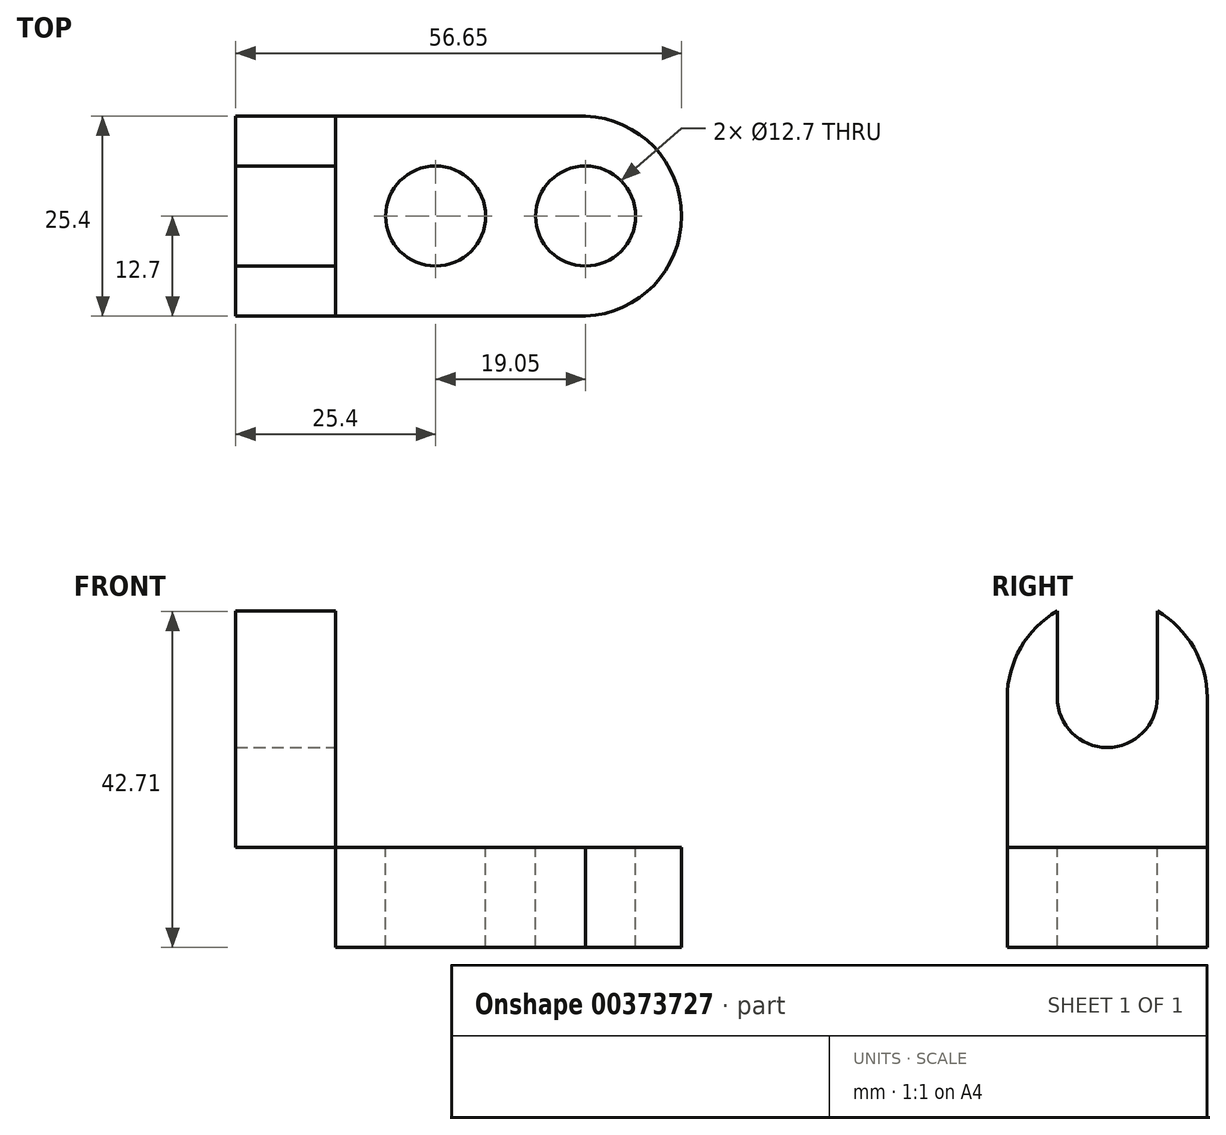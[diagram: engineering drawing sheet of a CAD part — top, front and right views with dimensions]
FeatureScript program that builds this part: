
annotation { "Feature Type Name" : "Feature", "Feature Type Description" : "" }
export const myFeature = defineFeature(function(context is Context, id is Id, definition is map)
    precondition{}
    {
        {
            var Q0;
            Q0=qCreatedBy(makeId("Front.planeOp"),FACE);
            var sketch = newSketch(context, id + "F0", { "sketchPlane" : qUnion([Q0])});
            skLineSegment(sketch, "E0.bottom", {"start": v(0, 0) * mm, "end": v(12.7, 0) * mm});
            skLineSegment(sketch, "E0.top", {"start": v(0, 44.45) * mm, "end": v(12.7, 44.45) * mm});
            skLineSegment(sketch, "E0.left", {"start": v(0, 0) * mm, "end": v(0, 44.45) * mm});
            skLineSegment(sketch, "E0.right", {"start": v(12.7, 0) * mm, "end": v(12.7, 44.45) * mm});
            skLineSegment(sketch, "E1.bottom", {"start": v(0, 0) * mm, "end": v(57.15, 0) * mm});
            skLineSegment(sketch, "E1.top", {"start": v(0, 12.7) * mm, "end": v(57.15, 12.7) * mm});
            skLineSegment(sketch, "E1.left", {"start": v(0, 0) * mm, "end": v(0, 12.7) * mm});
            skLineSegment(sketch, "E1.right", {"start": v(57.15, 0) * mm, "end": v(57.15, 12.7) * mm});
            skSolve(sketch);
        }
        {
            var Q0;
            {var subQ0=sQuery(id+"F0.wireOp",EDGE,"E0.top");Q0=makeQuery(id+"F0.imprint","IMPRINT",FACE,{"disambiguationData":[TD([[makeQuery(id+"F0.imprint","IMPRINT",EDGE,{"derivedFrom":subQ0}),-1.0]])]});}
            var Q1;
            {var subQ5=sQuery(id+"F0.wireOp",EDGE,"E1.left");Q1=makeQuery(id+"F0.imprint","IMPRINT",FACE,{"disambiguationData":[TD([[makeQuery(id+"F0.imprint","IMPRINT",EDGE,{"derivedFrom":subQ5}),-1.0]])]});}
            var Q2;
            {var subQ5=sQuery(id+"F0.wireOp",EDGE,"E1.right");Q2=makeQuery(id+"F0.imprint","IMPRINT",FACE,{"disambiguationData":[TD([[makeQuery(id+"F0.imprint","IMPRINT",EDGE,{"derivedFrom":subQ5}),1.0]])]});}
            extrude(context, id + "F1", {"entities" : qUnion([Q0, Q1, Q2]), "depth" : 25.4 * mm});
        }
        {
            var Q0;
            Q0=makeQuery(id+"F1.opExtrude","SWEPT_FACE",FACE,{"disambiguationData":[OSD([sQuery(id+"F0.wireOp",EDGE,"E1.top")])]});
            var sketch = newSketch(context, id + "F2", { "sketchPlane" : qUnion([Q0])});
            skCircle(sketch, "E2", {"center": v(25.4, -12.7) * mm, "radius": 6.35 * mm});
            skPoint(sketch, "E2.centerSnap0", {"position": v(12.7, -12.7) * mm});
            skCircle(sketch, "E3", {"center": v(44.45, -12.7) * mm, "radius": 6.35 * mm});
            skArc(sketch, "E4", {"start": v(44.45, -25.4) * mm, "mid": v(56.65, -12.7) * mm, "end": v(44.45, 0) * mm});
            skSolve(sketch);
        }
        {
            var Q0;
            Q0=makeQuery(id+"F2.imprint","IMPRINT",FACE,{"disambiguationData":[TD([[makeQuery(id+"F2.imprint","IMPRINT",EDGE,{"derivedFrom":sQuery(id+"F2.wireOp",EDGE,"E2")}),1.0]])]});
            var Q1;
            Q1=makeQuery(id+"F2.imprint","IMPRINT",FACE,{"disambiguationData":[TD([[makeQuery(id+"F2.imprint","IMPRINT",EDGE,{"derivedFrom":sQuery(id+"F2.wireOp",EDGE,"E3")}),1.0]])]});
            var Q2;
            {var subQ0=sQuery(id+"F2.wireOp",EDGE,"E4");Q2=makeQuery(id+"F2.imprint","IMPRINT",FACE,{"disambiguationData":[TD([[makeQuery(id+"F2.imprint","IMPRINT",EDGE,{"derivedFrom":subQ0}),-1.0]])]});}
            extrude(context, id + "F3", {"entities" : qUnion([Q0, Q1, Q2]), "operationType" : NewBodyOperationType.REMOVE, "oppositeDirection" : true, "depth" : 25.4 * mm});
        }
        {
            var Q0;
            Q0=makeQuery(id+"F1.opExtrude","SWEPT_FACE",FACE,{"disambiguationData":[OSD([sQuery(id+"F0.wireOp",EDGE,"E0.right")])]});
            var sketch = newSketch(context, id + "F4", { "sketchPlane" : qUnion([Q0])});
            skCircle(sketch, "E5", {"center": v(-12.7, 31.75) * mm, "radius": 6.35 * mm});
            skPoint(sketch, "E5.centerSnap0", {"position": v(-12.7, 12.7) * mm});
            skArc(sketch, "E6", {"start": v(0, 31.75) * mm, "mid": v(-12.7, 44.42) * mm, "end": v(-25.4, 31.75) * mm});
            skLineSegment(sketch, "E7", {"start": v(-19.05, 31.75) * mm, "end": v(-19.05, 44.45) * mm});
            skLineSegment(sketch, "E8", {"start": v(-6.35, 31.75) * mm, "end": v(-6.35, 44.45) * mm});
            skSolve(sketch);
        }
        {
            var Q0;
            {var subQ0=sQuery(id+"F4.wireOp",EDGE,"E5");var subQ1=makeQuery(id+"F4.imprint","INTERSECT",VERTEX,{"derivedFrom":[subQ0,sQuery(id+"F4.wireOp",EDGE,"E7")]});Q0=makeQuery(id+"F4.imprint","IMPRINT",FACE,{"disambiguationData":[TD([[makeQuery(id+"F4.imprint","IMPRINT",EDGE,{"disambiguationData":[TD([[subQ1,1.0]])],"derivedFrom":subQ0}),1.0]])]});}
            var Q1;
            {var subQ0=sQuery(id+"F4.wireOp",EDGE,"E7");var subQ1=sQuery(id+"F4.wireOp",EDGE,"E5");var subQ2=makeQuery(id+"F4.imprint","INTERSECT",VERTEX,{"derivedFrom":[subQ1,subQ0]});Q1=makeQuery(id+"F4.imprint","IMPRINT",FACE,{"disambiguationData":[TD([[makeQuery(id+"F4.imprint","IMPRINT",EDGE,{"disambiguationData":[TD([[subQ2,1.0]])],"derivedFrom":subQ1}),-1.0]])]});}
            var Q2;
            {var subQ0=sQuery(id+"F4.wireOp",EDGE,"E6");var subQ1=sQuery(id+"F0.wireOp",EDGE,"E0.right");var subQ2=makeQuery(id+"F1.opExtrude","CAP_EDGE",EDGE,{"disambiguationData":[OSD([subQ1])],"isStart":false});var subQ3=makeQuery(id+"F4.imprint","INTERSECT",VERTEX,{"derivedFrom":[subQ2,subQ0]});Q2=makeQuery(id+"F4.imprint","IMPRINT",FACE,{"disambiguationData":[TD([[makeQuery(id+"F4.imprint","IMPRINT",EDGE,{"disambiguationData":[TD([[subQ3,1.0]])],"derivedFrom":subQ0}),-1.0]])]});}
            var Q3;
            {var subQ0=sQuery(id+"F4.wireOp",EDGE,"E8");var subQ1=sQuery(id+"F4.wireOp",EDGE,"E6");var subQ2=makeQuery(id+"F4.imprint","INTERSECT",VERTEX,{"derivedFrom":[subQ1,subQ0]});Q3=makeQuery(id+"F4.imprint","IMPRINT",FACE,{"disambiguationData":[TD([[makeQuery(id+"F4.imprint","IMPRINT",EDGE,{"disambiguationData":[TD([[subQ2,-1.0]])],"derivedFrom":subQ1}),-1.0]])]});}
            var Q4;
            {var subQ0=sQuery(id+"F4.wireOp",EDGE,"E6");var subQ1=sQuery(id+"F0.wireOp",EDGE,"E0.right");var subQ2=makeQuery(id+"F1.opExtrude","CAP_EDGE",EDGE,{"disambiguationData":[OSD([subQ1])],"isStart":true});var subQ3=makeQuery(id+"F4.imprint","INTERSECT",VERTEX,{"derivedFrom":[subQ2,subQ0]});Q4=makeQuery(id+"F4.imprint","IMPRINT",FACE,{"disambiguationData":[TD([[makeQuery(id+"F4.imprint","IMPRINT",EDGE,{"disambiguationData":[TD([[subQ3,-1.0]])],"derivedFrom":subQ0}),-1.0]])]});}
            extrude(context, id + "F5", {"entities" : qUnion([Q0, Q1, Q2, Q3, Q4]), "operationType" : NewBodyOperationType.REMOVE, "oppositeDirection" : true, "depth" : 25.4 * mm});
        }
    });
